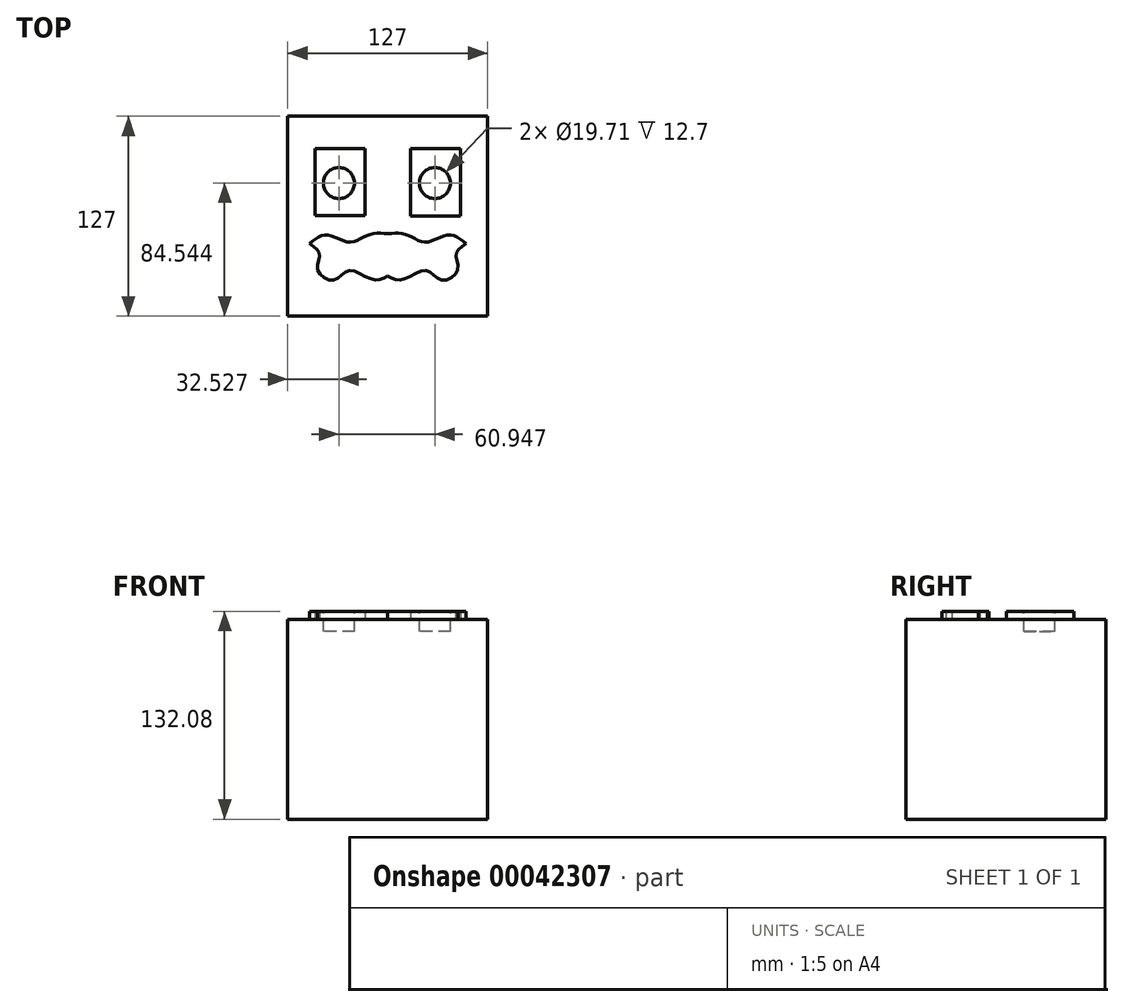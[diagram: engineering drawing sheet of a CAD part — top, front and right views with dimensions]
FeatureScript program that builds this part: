
annotation { "Feature Type Name" : "Feature", "Feature Type Description" : "" }
export const myFeature = defineFeature(function(context is Context, id is Id, definition is map)
    precondition{}
    {
        {
            var Q0;
            Q0=qCreatedBy(makeId("Top.planeOp"),FACE);
            var sketch = newSketch(context, id + "F0", { "sketchPlane" : qUnion([Q0])});
            skLineSegment(sketch, "E0.bottom", {"start": v(-63, 63.05) * mm, "end": v(64, 63.05) * mm});
            skLineSegment(sketch, "E0.top", {"start": v(-63, -63.95) * mm, "end": v(64, -63.95) * mm});
            skLineSegment(sketch, "E0.left", {"start": v(-63, 63.05) * mm, "end": v(-63, -63.95) * mm});
            skLineSegment(sketch, "E0.right", {"start": v(64, 63.05) * mm, "end": v(64, -63.95) * mm});
            skSolve(sketch);
        }
        {
            var Q0;
            Q0=makeQuery(id+"F0.imprint","IMPRINT",FACE,{"disambiguationData":[TD([[makeQuery(id+"F0.imprint","IMPRINT",EDGE,{"derivedFrom":sQuery(id+"F0.wireOp",EDGE,"E0.bottom")}),-1.0]])]});
            extrude(context, id + "F1", {"entities" : qUnion([Q0]), "depth" : 127 * mm});
        }
        {
            var Q0;
            Q0=makeQuery(id+"F1.opExtrude","CAP_FACE",FACE,{"disambiguationData":[OSD([sQuery(id+"F0.wireOp",EDGE,"E0.bottom"),sQuery(id+"F0.wireOp",EDGE,"E0.top"),sQuery(id+"F0.wireOp",EDGE,"E0.left"),sQuery(id+"F0.wireOp",EDGE,"E0.right")])],"isStart":false});
            var sketch = newSketch(context, id + "F2", { "sketchPlane" : qUnion([Q0])});
            skLineSegment(sketch, "E1", {"start": v(0.5, 63.05) * mm, "end": v(0.5, -63.95) * mm});
            skLineSegment(sketch, "E2", {"start": v(-63, 0) * mm, "end": v(64, -0.45) * mm});
            skLineSegment(sketch, "E3.bottom", {"start": v(14.89, -0.28) * mm, "end": v(46.61, -0.28) * mm});
            skLineSegment(sketch, "E3.top", {"start": v(14.89, 42.58) * mm, "end": v(46.61, 42.58) * mm});
            skLineSegment(sketch, "E3.left", {"start": v(14.89, -0.28) * mm, "end": v(14.89, 42.58) * mm});
            skLineSegment(sketch, "E3.right", {"start": v(46.61, -0.28) * mm, "end": v(46.61, 42.58) * mm});
            skLineSegment(sketch, "E4.MirrorCS", {"start": v(-13.88, -0.28) * mm, "end": v(-13.88, 42.58) * mm});
            skLineSegment(sketch, "E5.MirrorCS", {"start": v(-13.88, 42.58) * mm, "end": v(-45.6, 42.58) * mm});
            skLineSegment(sketch, "E6.MirrorCS", {"start": v(-45.6, -0.28) * mm, "end": v(-45.6, 42.58) * mm});
            skLineSegment(sketch, "E7.MirrorCS", {"start": v(-13.88, -0.28) * mm, "end": v(-45.6, -0.28) * mm});
            skFitSpline(sketch, "E8", {"points": [v(-49.12, -17.95) * mm, v(-38.4, -12.38) * mm, v(-23.66, -16.98) * mm, v(-11.97, -12.38) * mm, v(0.5, -11.55) * mm], "startDerivative": vector(41.68, 36.17) * mm, "endDerivative": vector(52.6, -3.82) * mm});
            skFitSpline(sketch, "E9", {"points": [v(-49.12, -17.95) * mm, v(-42.86, -24.63) * mm, v(-43.83, -34.79) * mm, v(-33.81, -41.05) * mm, v(-24.07, -34.93) * mm, v(-9.04, -40.63) * mm, v(0.5, -38.54) * mm], "startDerivative": vector(58.75, -39.26) * mm, "endDerivative": vector(56.68, 29.2) * mm});
            skFitSpline(sketch, "E10.MirrorCS", {"points": [v(50.13, -17.95) * mm, v(39.41, -12.38) * mm, v(24.66, -16.98) * mm, v(12.97, -12.38) * mm, v(0.5, -11.55) * mm], "startDerivative": vector(-41.68, 36.17) * mm, "endDerivative": vector(-52.6, -3.82) * mm});
            skFitSpline(sketch, "E11.MirrorCS", {"points": [v(50.13, -17.95) * mm, v(43.86, -24.63) * mm, v(44.84, -34.79) * mm, v(34.82, -41.05) * mm, v(25.08, -34.93) * mm, v(10.05, -40.63) * mm, v(0.5, -38.54) * mm], "startDerivative": vector(-58.75, -39.26) * mm, "endDerivative": vector(-56.68, 29.2) * mm});
            skSolve(sketch);
        }
        {
            var Q0;
            {var subQ3=sQuery(id+"F2.wireOp",EDGE,"E5.MirrorCS");Q0=makeQuery(id+"F2.imprint","IMPRINT",FACE,{"disambiguationData":[TD([[makeQuery(id+"F2.imprint","IMPRINT",EDGE,{"derivedFrom":subQ3}),1.0]])]});}
            var Q1;
            Q1=makeQuery(id+"F2.imprint","IMPRINT",FACE,{"disambiguationData":[TD([[makeQuery(id+"F2.imprint","IMPRINT",EDGE,{"derivedFrom":sQuery(id+"F2.wireOp",EDGE,"E3.bottom")}),1.0]])]});
            var Q2;
            {var subQ1=sQuery(id+"F2.wireOp",EDGE,"E10.MirrorCS");Q2=makeQuery(id+"F2.imprint","IMPRINT",FACE,{"disambiguationData":[TD([[makeQuery(id+"F2.imprint","IMPRINT",EDGE,{"derivedFrom":subQ1}),1.0]])]});}
            var Q3;
            {var subQ1=sQuery(id+"F2.wireOp",EDGE,"E8");Q3=makeQuery(id+"F2.imprint","IMPRINT",FACE,{"disambiguationData":[TD([[makeQuery(id+"F2.imprint","IMPRINT",EDGE,{"derivedFrom":subQ1}),-1.0]])]});}
            extrude(context, id + "F3", {"entities" : qUnion([Q0, Q1, Q2, Q3]), "operationType" : NewBodyOperationType.ADD, "depth" : 5.08 * mm});
        }
        {
            var Q0;
            Q0=makeQuery(id+"F3.opExtrude","CAP_FACE",FACE,{"disambiguationData":[OSD([sQuery(id+"F2.wireOp",EDGE,"E2"),sQuery(id+"F2.wireOp",EDGE,"E4.MirrorCS"),sQuery(id+"F2.wireOp",EDGE,"E5.MirrorCS"),sQuery(id+"F2.wireOp",EDGE,"E6.MirrorCS")])],"isStart":false});
            var sketch = newSketch(context, id + "F4", { "sketchPlane" : qUnion([Q0])});
            skCircle(sketch, "E12", {"center": v(-30.28, 20.58) * mm, "radius": 9.76 * mm});
            skSolve(sketch);
        }
        {
            var Q0;
            Q0=makeQuery(id+"F4.imprint","IMPRINT",FACE,{"disambiguationData":[TD([[makeQuery(id+"F4.imprint","IMPRINT",EDGE,{"derivedFrom":sQuery(id+"F4.wireOp",EDGE,"E12")}),-1.0]])]});
            cPlane(context, id + "F5", {"entities" : qUnion([Q0]), "cplaneType" : CPlaneType.OFFSET, "offset" : 152.4 * mm, "width" : 152.4 * mm, "height" : 152.4 * mm});
        }
        {
            var Q0;
            Q0=qCreatedBy(id+"F5.planeOp",FACE);
            var sketch = newSketch(context, id + "F6", { "sketchPlane" : qUnion([Q0])});
            skCircle(sketch, "E13", {"center": v(-30.47, 20.6) * mm, "radius": 9.86 * mm});
            skCircle(sketch, "E14.MirrorC", {"center": v(30.47, 20.6) * mm, "radius": 9.86 * mm});
            skPoint(sketch, "E15.start.orphan", {"position": v(0, 61.64) * mm});
            skSolve(sketch);
        }
        {
            var Q0;
            Q0 = qSketchRegion(id + "F6", true);
            extrude(context, id + "F7", {"entities" : qUnion([Q0]), "operationType" : NewBodyOperationType.REMOVE, "oppositeDirection" : true, "depth" : 165.1 * mm});
        }
    });
